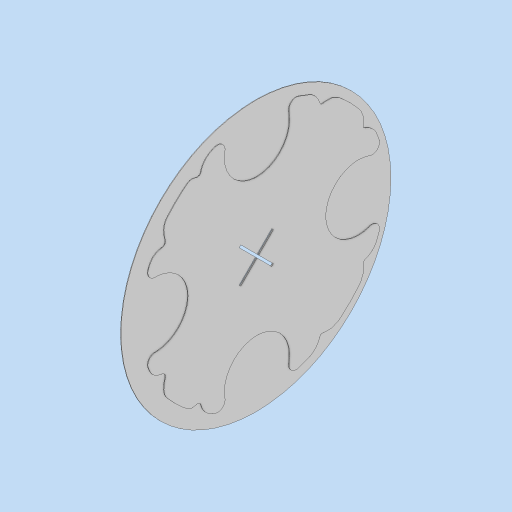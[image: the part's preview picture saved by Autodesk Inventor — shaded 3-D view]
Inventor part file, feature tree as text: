
AUTODESK INVENTOR PART (.ipt)
format: ipt  version: 2024 (Build 280153000, 153)  size: 1,135,616 bytes
history: native  units: mm
features: extrude x3, sketch x1
ambient origin geometry x8: Origin, YZ Plane, XZ Plane, XY Plane, X Axis, Y Axis, Z Axis, Center Point
bodies: Solid1 (feature_tree)
feature tree (4):
  sketch  "Sketch1"  dims[d0=0.25mm d1=0.0mm d2=0.5mm d3=0.0mm d4=0.5mm d5=0.5mm d6=0.5mm d7=0.5mm d8=0.0mm d9=0.0mm]
  extrude  "Extrusion1"  Depth=0.5mm TaperAngle=0.0deg
  extrude  "Extrusion2"  Depth=0.5mm
  extrude  "Extrusion3"  Depth=0.5mm
